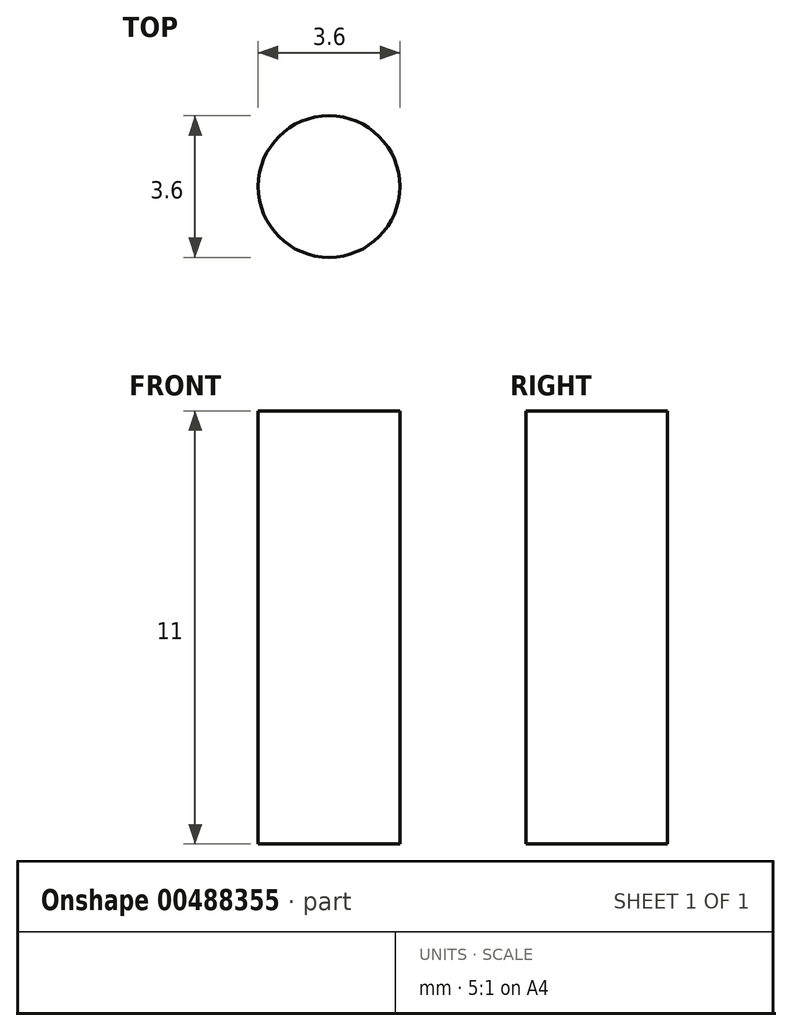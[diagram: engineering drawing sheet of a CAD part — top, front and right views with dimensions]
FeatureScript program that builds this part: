
annotation { "Feature Type Name" : "Feature", "Feature Type Description" : "" }
export const myFeature = defineFeature(function(context is Context, id is Id, definition is map)
    precondition{}
    {
        {
            var Q0;
            Q0=qCreatedBy(makeId("Top.planeOp"),FACE);
            var sketch = newSketch(context, id + "F0", { "sketchPlane" : qUnion([Q0])});
            skCircle(sketch, "E0", {"center": v(0, 0) * mm, "radius": 1.8 * mm});
            skSolve(sketch);
        }
        {
            var Q0;
            Q0 = qSketchRegion(id + "F0", true);
            extrude(context, id + "F1", {"entities" : qUnion([Q0]), "endBound" : BoundingType.SYMMETRIC, "depth" : 11 * mm});
        }
    });
